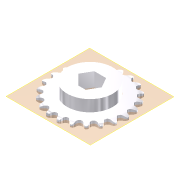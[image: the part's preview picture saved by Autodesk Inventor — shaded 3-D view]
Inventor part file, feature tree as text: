
AUTODESK INVENTOR PART (.ipt)
format: ipt  version: 2013 (Build 170138000, 138)  size: 664,064 bytes
history: native  units: mm
features: other x6, extrude x4, sketch x2, pattern_linear x1, pattern_circular x1
ambient origin geometry x8: Origin, YZ Plane, XZ Plane, XY Plane, X Axis, Y Axis, Z Axis, Center Point
bodies: Solid1 (feature_tree)
feature tree (14):
  other  "Theoretical Tooth Profile"
  other  "Tooth Profile"
  other  "Section Profile"
  other  "Shroud"
  other  "Strand"
  pattern_linear  "Strand Pattern"  Spacing1=1.697355mm  [1 undecoded]
  extrude  "Theoretical Tooth"  Depth=22.292615mm
  extrude  "Tooth"  Depth=2.697327mm
  pattern_circular  "Tooth Pattern"  [2 undecoded]
  other  "Timing Plane"
  extrude  "Extrusion4"  Depth=4.338955mm
  extrude  "Extrusion6"  Depth=4.6228mm
  sketch  "Sketch4"  dims[d0=44.619381mm]
  sketch  "Sketch6"  dims[d2=2.855993mm d3=1.697355mm d10=22.292615mm d11=2.697327mm d12=2.6416mm d13=4.338955mm d14=4.6228mm d18=10.0mm d19=0.0mm d20=220.0mm d21=360.0deg d23=1.905mm d28=0.0mm d29=0.0mm d30=3.1242mm d31=36.54522mm d32=3.1242mm d33=0.79375mm d34=6.75005mm d36=90.0deg d37=90.0deg d38=10.0mm d40=6.4008mm d42=0.0mm d43=1.5621mm d44=23.720612mm d45=1.697355mm d46=9.50976mm d47=0.0mm d48=25.4mm d49=0.0mm d50=10.0mm d51=12.7mm d52=28.575mm d53=7.1628mm d54=0.0mm d60=12.7762mm d61=25.4mm d62=0.0mm]
note: 3 required parameter values undecoded (feature->parameter linkage not recoverable at this tier; creation-order binding heuristic only, values carry confidence <= 0.55)
